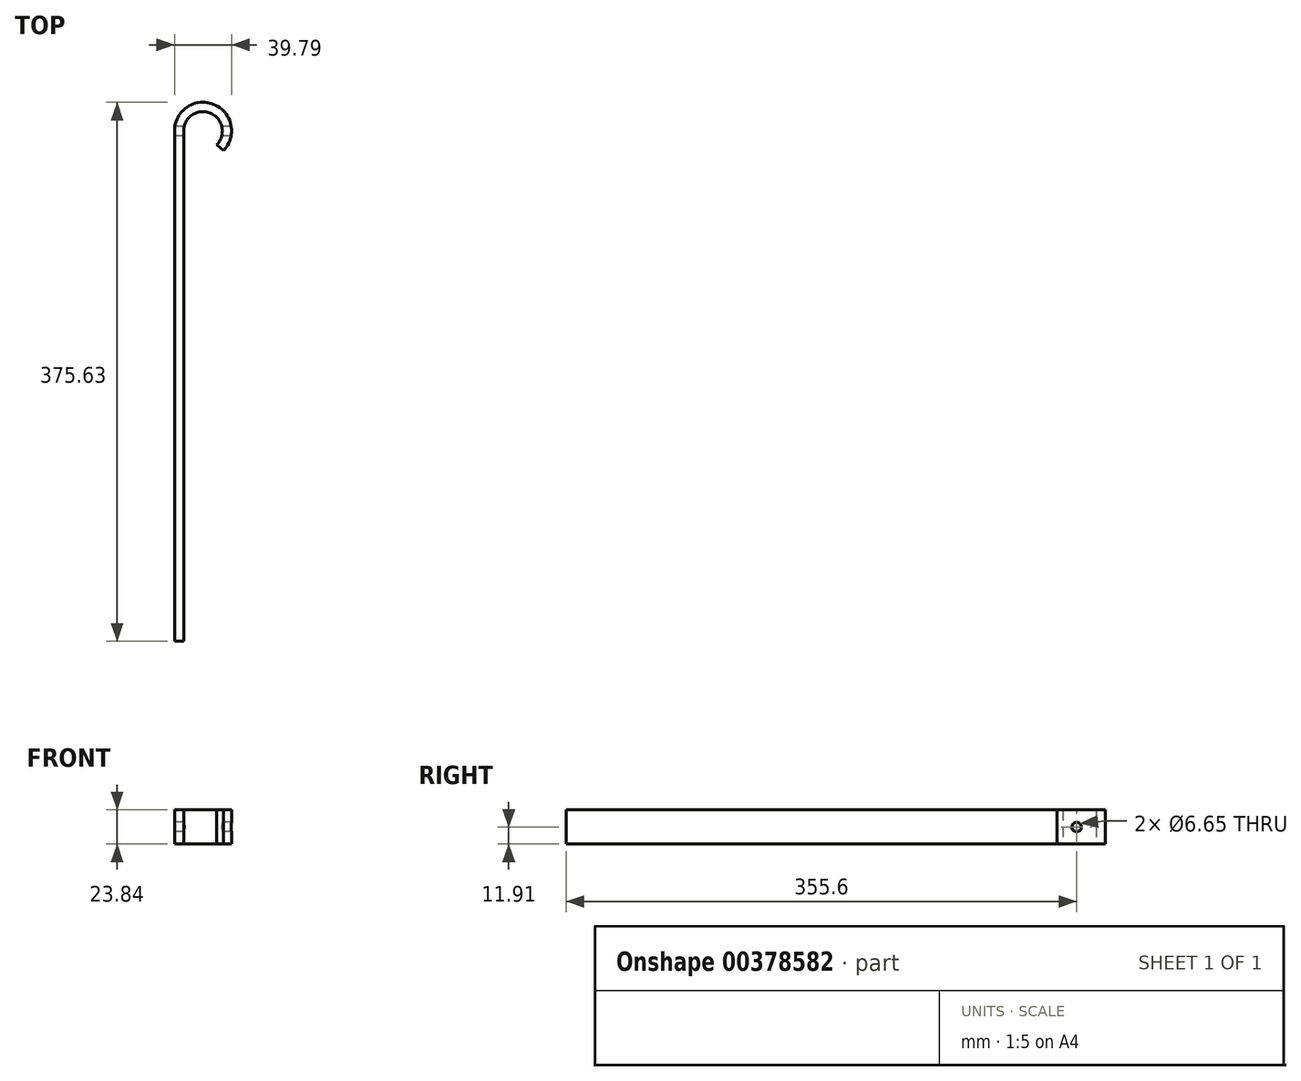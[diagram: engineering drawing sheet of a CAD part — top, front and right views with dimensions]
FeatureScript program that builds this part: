
annotation { "Feature Type Name" : "Feature", "Feature Type Description" : "" }
export const myFeature = defineFeature(function(context is Context, id is Id, definition is map)
    precondition{}
    {
        {
            var Q0;
            Q0=qCreatedBy(makeId("Top.planeOp"),FACE);
            var sketch = newSketch(context, id + "F0", { "sketchPlane" : qUnion([Q0])});
            skLineSegment(sketch, "E0", {"start": v(-13.5, 0) * mm, "end": v(-13.5, -355.6) * mm});
            skArc(sketch, "E1", {"start": v(19.94, 0) * mm, "mid": v(0.04, 20.03) * mm, "end": v(-19.85, 0) * mm});
            skLineSegment(sketch, "E2", {"start": v(-19.85, 0) * mm, "end": v(-19.85, -355.6) * mm});
            skLineSegment(sketch, "E3", {"start": v(-19.85, -355.6) * mm, "end": v(-13.5, -355.6) * mm});
            skArc(sketch, "E4", {"start": v(-19.85, 0) * mm, "mid": v(7.46, 18.6) * mm, "end": v(14.32, -13.72) * mm});
            skArc(sketch, "E5", {"start": v(-13.5, 0) * mm, "mid": v(5.14, 12.48) * mm, "end": v(9.58, -9.51) * mm});
            skLineSegment(sketch, "E6", {"start": v(9.58, -9.51) * mm, "end": v(14.32, -13.72) * mm});
            skSolve(sketch);
        }
        {
            var Q0;
            Q0 = qSketchRegion(id + "F0", true);
            extrude(context, id + "F1", {"entities" : qUnion([Q0]), "depth" : 11.93 * mm, "hasSecondDirection" : true, "secondDirectionOppositeDirection" : true, "secondDirectionDepth" : 11.9 * mm});
        }
        {
            var Q0;
            Q0=qCreatedBy(makeId("Right.planeOp"),FACE);
            var sketch = newSketch(context, id + "F2", { "sketchPlane" : qUnion([Q0])});
            skCircle(sketch, "E7", {"center": v(0, 0) * mm, "radius": 3.33 * mm});
            skSolve(sketch);
        }
        {
            var Q0;
            Q0 = qSketchRegion(id + "F2", true);
            extrude(context, id + "F3", {"entities" : qUnion([Q0]), "operationType" : NewBodyOperationType.REMOVE, "depth" : 25.4 * mm, "hasSecondDirection" : true, "secondDirectionOppositeDirection" : true, "secondDirectionDepth" : 25.4 * mm});
        }
    });
